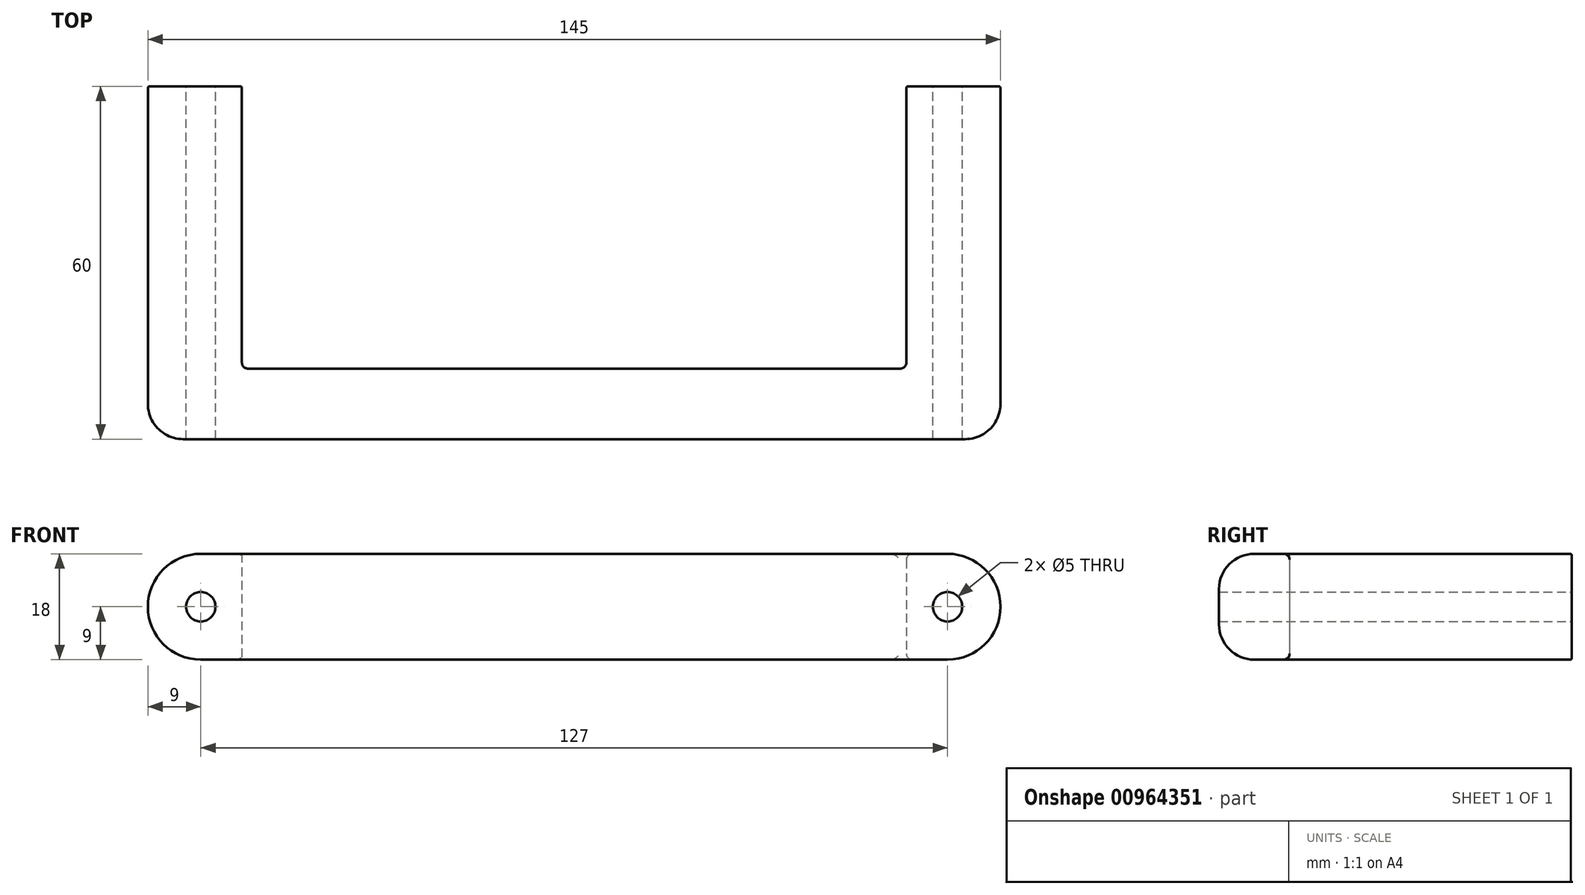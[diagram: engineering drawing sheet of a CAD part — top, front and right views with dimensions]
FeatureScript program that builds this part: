
annotation { "Feature Type Name" : "Feature", "Feature Type Description" : "" }
export const myFeature = defineFeature(function(context is Context, id is Id, definition is map)
    precondition{}
    {
        {
            var Q0;
            Q0=qCreatedBy(makeId("Front.planeOp"),FACE);
            var sketch = newSketch(context, id + "F0", { "sketchPlane" : qUnion([Q0])});
            skLineSegment(sketch, "E0.bottom", {"start": v(0, 0) * mm, "end": v(-127, 0) * mm});
            skLineSegment(sketch, "E0.top", {"start": v(0, 18) * mm, "end": v(-127, 18) * mm});
            skLineSegment(sketch, "E0.left", {"start": v(0, 0) * mm, "end": v(0, 18) * mm});
            skLineSegment(sketch, "E0.right", {"start": v(-127, 0) * mm, "end": v(-127, 18) * mm});
            skLineSegment(sketch, "E1", {"start": v(-127, 9) * mm, "end": v(0, 9) * mm, "construction": true});
            skLineSegment(sketch, "E2", {"start": v(-120, 18) * mm, "end": v(-120, 0) * mm, "construction": true});
            skLineSegment(sketch, "E3", {"start": v(-120, 0) * mm, "end": v(-7, 18) * mm, "construction": true});
            skLineSegment(sketch, "E4", {"start": v(-7, 18) * mm, "end": v(-7, 0) * mm, "construction": true});
            skPoint(sketch, "E5", {"position": v(-63.5, 9) * mm});
            skPoint(sketch, "E5.positionSnap0", {"position": v(-63.5, 9) * mm});
            skCircle(sketch, "E6", {"center": v(-127, 9) * mm, "radius": 9 * mm});
            skCircle(sketch, "E7", {"center": v(0, 9) * mm, "radius": 9 * mm});
            skCircle(sketch, "E8", {"center": v(-127, 9) * mm, "radius": 2.5 * mm});
            skCircle(sketch, "E9", {"center": v(0, 9) * mm, "radius": 2.5 * mm});
            skCircle(sketch, "E10", {"center": v(0, 9) * mm, "radius": 6 * mm});
            skCircle(sketch, "E11", {"center": v(-127, 9) * mm, "radius": 6 * mm});
            skLineSegment(sketch, "E12", {"start": v(-127, 15) * mm, "end": v(0, 15) * mm, "construction": true});
            skLineSegment(sketch, "E13", {"start": v(-127, 11.5) * mm, "end": v(0, 11.5) * mm, "construction": true});
            skSolve(sketch);
        }
        {
            var Q0;
            {var subQ0=sQuery(id+"F0.wireOp",EDGE,"E0.bottom");Q0=makeQuery(id+"F0.imprint","IMPRINT",FACE,{"disambiguationData":[TD([[makeQuery(id+"F0.imprint","IMPRINT",EDGE,{"derivedFrom":subQ0}),-1.0]])]});}
            var Q1;
            {var subQ1=sQuery(id+"F0.wireOp",EDGE,"E0.right");var subQ3=sQuery(id+"F0.wireOp",EDGE,"E11");var subQ4=makeQuery(id+"F0.imprint","INTERSECT",VERTEX,{"disambiguationData":[OD(0.0)],"derivedFrom":[subQ1,subQ3]});Q1=makeQuery(id+"F0.imprint","IMPRINT",FACE,{"disambiguationData":[TD([[makeQuery(id+"F0.imprint","IMPRINT",EDGE,{"disambiguationData":[TD([[subQ4,1.0]])],"derivedFrom":subQ3}),-1.0]])]});}
            var Q2;
            {var subQ1=sQuery(id+"F0.wireOp",EDGE,"E0.right");var subQ3=sQuery(id+"F0.wireOp",EDGE,"E11");var subQ4=makeQuery(id+"F0.imprint","INTERSECT",VERTEX,{"disambiguationData":[OD(0.0)],"derivedFrom":[subQ1,subQ3]});Q2=makeQuery(id+"F0.imprint","IMPRINT",FACE,{"disambiguationData":[TD([[makeQuery(id+"F0.imprint","IMPRINT",EDGE,{"disambiguationData":[TD([[subQ4,-1.0]])],"derivedFrom":subQ3}),-1.0]])]});}
            var Q3;
            {var subQ1=sQuery(id+"F0.wireOp",EDGE,"E0.left");var subQ3=sQuery(id+"F0.wireOp",EDGE,"E10");var subQ4=makeQuery(id+"F0.imprint","INTERSECT",VERTEX,{"disambiguationData":[OD(0.0)],"derivedFrom":[subQ1,subQ3]});Q3=makeQuery(id+"F0.imprint","IMPRINT",FACE,{"disambiguationData":[TD([[makeQuery(id+"F0.imprint","IMPRINT",EDGE,{"disambiguationData":[TD([[subQ4,1.0]])],"derivedFrom":subQ3}),-1.0]])]});}
            var Q4;
            {var subQ1=sQuery(id+"F0.wireOp",EDGE,"E0.left");var subQ3=sQuery(id+"F0.wireOp",EDGE,"E10");var subQ4=makeQuery(id+"F0.imprint","INTERSECT",VERTEX,{"disambiguationData":[OD(0.0)],"derivedFrom":[subQ1,subQ3]});Q4=makeQuery(id+"F0.imprint","IMPRINT",FACE,{"disambiguationData":[TD([[makeQuery(id+"F0.imprint","IMPRINT",EDGE,{"disambiguationData":[TD([[subQ4,-1.0]])],"derivedFrom":subQ3}),-1.0]])]});}
            var Q5;
            {var subQ0=sQuery(id+"F0.wireOp",EDGE,"E10");var subQ1=sQuery(id+"F0.wireOp",EDGE,"E0.left");var subQ2=makeQuery(id+"F0.imprint","INTERSECT",VERTEX,{"disambiguationData":[OD(0.0)],"derivedFrom":[subQ1,subQ0]});Q5=makeQuery(id+"F0.imprint","IMPRINT",FACE,{"disambiguationData":[TD([[makeQuery(id+"F0.imprint","IMPRINT",EDGE,{"disambiguationData":[TD([[subQ2,-1.0]])],"derivedFrom":subQ1}),-1.0]])]});}
            var Q6;
            {var subQ0=sQuery(id+"F0.wireOp",EDGE,"E10");var subQ1=sQuery(id+"F0.wireOp",EDGE,"E0.left");var subQ2=makeQuery(id+"F0.imprint","INTERSECT",VERTEX,{"disambiguationData":[OD(0.0)],"derivedFrom":[subQ1,subQ0]});Q6=makeQuery(id+"F0.imprint","IMPRINT",FACE,{"disambiguationData":[TD([[makeQuery(id+"F0.imprint","IMPRINT",EDGE,{"disambiguationData":[TD([[subQ2,-1.0]])],"derivedFrom":subQ1}),1.0]])]});}
            var Q7;
            {var subQ0=sQuery(id+"F0.wireOp",EDGE,"E11");var subQ1=sQuery(id+"F0.wireOp",EDGE,"E0.right");var subQ2=makeQuery(id+"F0.imprint","INTERSECT",VERTEX,{"disambiguationData":[OD(0.0)],"derivedFrom":[subQ1,subQ0]});Q7=makeQuery(id+"F0.imprint","IMPRINT",FACE,{"disambiguationData":[TD([[makeQuery(id+"F0.imprint","IMPRINT",EDGE,{"disambiguationData":[TD([[subQ2,-1.0]])],"derivedFrom":subQ1}),-1.0]])]});}
            var Q8;
            {var subQ0=sQuery(id+"F0.wireOp",EDGE,"E11");var subQ1=sQuery(id+"F0.wireOp",EDGE,"E0.right");var subQ2=makeQuery(id+"F0.imprint","INTERSECT",VERTEX,{"disambiguationData":[OD(0.0)],"derivedFrom":[subQ1,subQ0]});Q8=makeQuery(id+"F0.imprint","IMPRINT",FACE,{"disambiguationData":[TD([[makeQuery(id+"F0.imprint","IMPRINT",EDGE,{"disambiguationData":[TD([[subQ2,-1.0]])],"derivedFrom":subQ1}),1.0]])]});}
            extrude(context, id + "F1", {"entities" : qUnion([Q0, Q1, Q2, Q3, Q4, Q5, Q6, Q7, Q8]), "depth" : 60 * mm, "offsetDistance" : 25 * mm});
        }
        {
            var Q0;
            Q0=makeQuery(id+"F1.opExtrude","SWEPT_FACE",FACE,{"disambiguationData":[OSD([sQuery(id+"F0.wireOp",EDGE,"E0.bottom")])]});
            var sketch = newSketch(context, id + "F2", { "sketchPlane" : qUnion([Q0])});
            skPoint(sketch, "E14.0", {"position": v(-120, 0) * mm});
            skPoint(sketch, "E15.0", {"position": v(-7, 0) * mm});
            skLineSegment(sketch, "E16.bottom", {"start": v(-120, 0) * mm, "end": v(-7, 0) * mm});
            skLineSegment(sketch, "E16.top", {"start": v(-120, 48) * mm, "end": v(-7, 48) * mm});
            skLineSegment(sketch, "E16.left", {"start": v(-120, 0) * mm, "end": v(-120, 48) * mm});
            skLineSegment(sketch, "E16.right", {"start": v(-7, 0) * mm, "end": v(-7, 48) * mm});
            skSolve(sketch);
        }
        {
            var Q0;
            Q0 = qSketchRegion(id + "F2", true);
            extrude(context, id + "F3", {"entities" : qUnion([Q0]), "operationType" : NewBodyOperationType.REMOVE, "endBound" : BoundingType.THROUGH_ALL, "oppositeDirection" : true, "depth" : 25 * mm, "offsetDistance" : 25 * mm});
        }
        {
            var Q0;
            Q0=makeQuery(id+"F1.opExtrude","CAP_EDGE",EDGE,{"disambiguationData":[OSD([sQuery(id+"F0.wireOp",EDGE,"E9")])],"isStart":true});
            var Q1;
            Q1=makeQuery(id+"F1.opExtrude","CAP_EDGE",EDGE,{"disambiguationData":[OSD([sQuery(id+"F0.wireOp",EDGE,"E8")])],"isStart":true});
            var Q2;
            {var subQ0=sQuery(id+"F0.wireOp",EDGE,"E9");var subQ1=sQuery(id+"F0.wireOp",EDGE,"E0.top");var subQ2=sQuery(id+"F0.wireOp",EDGE,"E7");var subQ3=sQuery(id+"F0.wireOp",EDGE,"E0.bottom");Q2=makeQuery(id+"F3.boolean.opBoolean","SPLIT",FACE,{"disambiguationData":[TD([makeQuery(id+"F1.opExtrude","SWEPT_FACE",FACE,{"disambiguationData":[OSD([subQ2])]})])],"derivedFrom":makeQuery(id+"F1.opExtrude","CAP_FACE",FACE,{"disambiguationData":[OSD([subQ3,subQ1,sQuery(id+"F0.wireOp",EDGE,"E6"),subQ2,sQuery(id+"F0.wireOp",EDGE,"E8"),subQ0])],"isStart":true})});}
            var Q3;
            {var subQ0=sQuery(id+"F0.wireOp",EDGE,"E8");var subQ1=sQuery(id+"F0.wireOp",EDGE,"E6");var subQ2=sQuery(id+"F0.wireOp",EDGE,"E0.top");var subQ3=sQuery(id+"F0.wireOp",EDGE,"E0.bottom");Q3=makeQuery(id+"F3.boolean.opBoolean","SPLIT",FACE,{"disambiguationData":[TD([makeQuery(id+"F1.opExtrude","SWEPT_FACE",FACE,{"disambiguationData":[OSD([subQ1])]})])],"derivedFrom":makeQuery(id+"F1.opExtrude","CAP_FACE",FACE,{"disambiguationData":[OSD([subQ3,subQ2,subQ1,sQuery(id+"F0.wireOp",EDGE,"E7"),subQ0,sQuery(id+"F0.wireOp",EDGE,"E9")])],"isStart":true})});}
            fillet(context, id + "F4", {"entities" : qUnion([Q0, Q1, Q2, Q3]), "tangentPropagation" : true, "radius" : .3 * mm, "defaultsChanged" : false, "vertexSettings" : [], "allowEdgeOverflow" : false});
        }
        {
            var Q0;
            Q0=makeQuery(id+"F3.boolean.opBoolean","COPY",EDGE,{"derivedFrom":makeQuery(id+"F3.opExtrude","SWEPT_EDGE",EDGE,{"disambiguationData":[OSD([sQuery(id+"F2.wireOp",EDGE,"E16.top"),sQuery(id+"F2.wireOp",EDGE,"E16.left")])]})});
            var Q1;
            Q1=makeQuery(id+"F3.boolean.opBoolean","COPY",EDGE,{"derivedFrom":makeQuery(id+"F3.opExtrude","SWEPT_EDGE",EDGE,{"disambiguationData":[OSD([sQuery(id+"F2.wireOp",EDGE,"E16.top"),sQuery(id+"F2.wireOp",EDGE,"E16.right")])]})});
            var Q2;
            Q2=makeQuery(id+"F3.boolean.opBoolean","COPY",FACE,{"derivedFrom":makeQuery(id+"F3.opExtrude","SWEPT_FACE",FACE,{"disambiguationData":[OSD([sQuery(id+"F2.wireOp",EDGE,"E16.right")])]})});
            fillet(context, id + "F5", {"entities" : qUnion([Q0, Q1, Q2]), "tangentPropagation" : true, "radius" : 1 * mm, "defaultsChanged" : false, "vertexSettings" : [], "allowEdgeOverflow" : false});
        }
        {
            var Q0;
            Q0=makeQuery(id+"F1.opExtrude","CAP_EDGE",EDGE,{"disambiguationData":[OSD([sQuery(id+"F0.wireOp",EDGE,"E7")])],"isStart":false});
            fillet(context, id + "F6", {"entities" : qUnion([Q0]), "tangentPropagation" : true, "radius" : 6 * mm, "defaultsChanged" : true, "vertexSettings" : [], "allowEdgeOverflow" : false});
        }
    });
